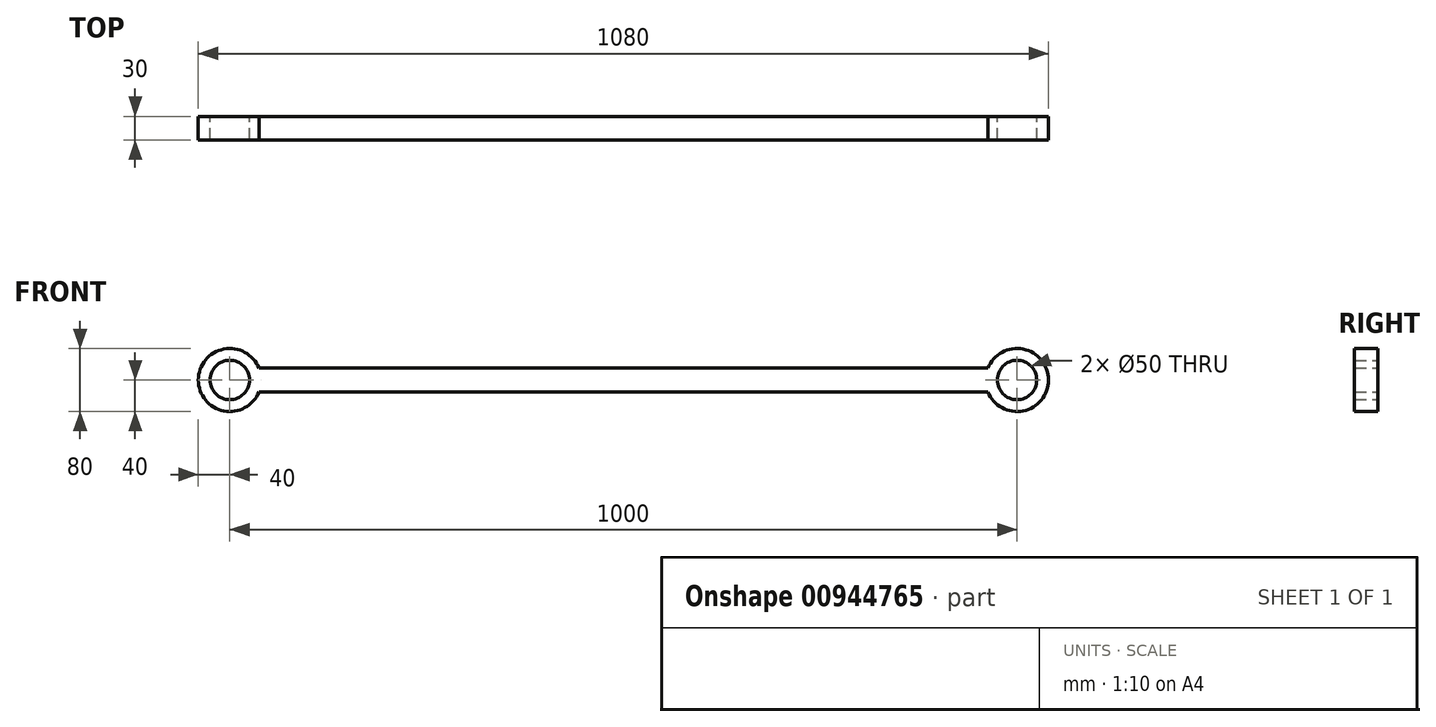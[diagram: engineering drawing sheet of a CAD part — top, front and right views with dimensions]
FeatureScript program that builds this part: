
annotation { "Feature Type Name" : "Feature", "Feature Type Description" : "" }
export const myFeature = defineFeature(function(context is Context, id is Id, definition is map)
    precondition{}
    {
        {
            var Q0;
            Q0=qCreatedBy(makeId("Front.planeOp"),FACE);
            var sketch = newSketch(context, id + "F0", { "sketchPlane" : qUnion([Q0])});
            skCircle(sketch, "E0", {"center": v(-500, 0) * mm, "radius": 25 * mm});
            skCircle(sketch, "E1", {"center": v(500, 0) * mm, "radius": 25 * mm});
            skArc(sketch, "E2", {"start": v(-462.92, 15) * mm, "mid": v(-540, 0) * mm, "end": v(-462.92, -15) * mm});
            skArc(sketch, "E3", {"start": v(462.92, -15) * mm, "mid": v(540, 0) * mm, "end": v(462.92, 15) * mm});
            skLineSegment(sketch, "E4.bottom", {"start": v(462.92, -15) * mm, "end": v(-462.92, -15) * mm});
            skLineSegment(sketch, "E4.top", {"start": v(462.92, 15) * mm, "end": v(-462.92, 15) * mm});
            skLineSegment(sketch, "E4.left", {"start": v(462.92, -15) * mm, "end": v(462.92, 15) * mm, "construction": true});
            skLineSegment(sketch, "E4.right", {"start": v(-462.92, -15) * mm, "end": v(-462.92, 15) * mm, "construction": true});
            skPoint(sketch, "E4.middle", {"position": v(0, 0) * mm});
            skLineSegment(sketch, "E5", {"start": v(-250.43, 0) * mm, "end": v(205.1, 0) * mm, "construction": true});
            skSolve(sketch);
        }
        {
            var Q0;
            Q0=qSketchRegion(id+"F0",true);
            extrude(context, id + "F1", {"entities" : qUnion([Q0]), "endBound" : BoundingType.SYMMETRIC, "depth" : 30 * mm, "offsetDistance" : 25 * mm});
        }
    });
